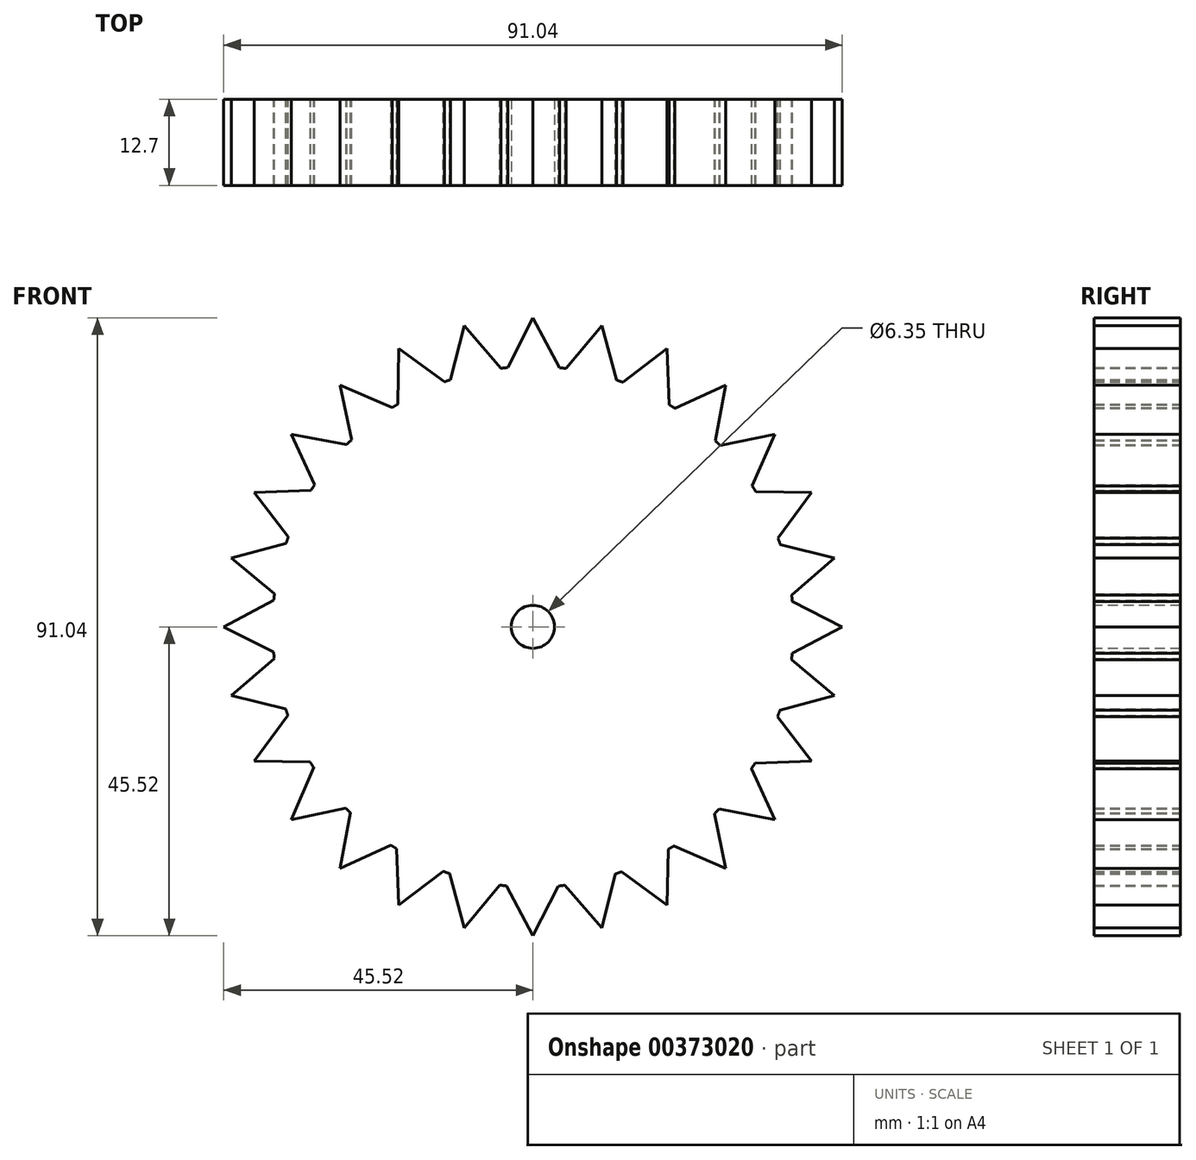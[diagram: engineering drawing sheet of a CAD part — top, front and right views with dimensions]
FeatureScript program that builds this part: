
annotation { "Feature Type Name" : "Feature", "Feature Type Description" : "" }
export const myFeature = defineFeature(function(context is Context, id is Id, definition is map)
    precondition{}
    {
        {
            var Q0;
            Q0=qCreatedBy(makeId("Front.planeOp"),FACE);
            var sketch = newSketch(context, id + "F0", { "sketchPlane" : qUnion([Q0])});
            skCircle(sketch, "E0", {"center": v(0, 0) * mm, "radius": 38.36 * mm});
            skLineSegment(sketch, "E1", {"start": v(-3.71, 38.18) * mm, "end": v(0, 45.52) * mm});
            skLineSegment(sketch, "E2", {"start": v(0, 45.52) * mm, "end": v(3.9, 38.16) * mm});
            skLineSegment(sketch, "E3.1.0", {"start": v(-10.13, 44.38) * mm, "end": v(-4.69, 38.08) * mm});
            skLineSegment(sketch, "E3.1.1", {"start": v(-12.12, 36.4) * mm, "end": v(-10.13, 44.38) * mm});
            skLineSegment(sketch, "E3.2.0", {"start": v(-19.75, 41.01) * mm, "end": v(-13.04, 36.08) * mm});
            skLineSegment(sketch, "E3.2.1", {"start": v(-19.91, 32.8) * mm, "end": v(-19.75, 41.01) * mm});
            skLineSegment(sketch, "E3.3.0", {"start": v(-28.38, 35.6) * mm, "end": v(-20.74, 32.27) * mm});
            skLineSegment(sketch, "E3.3.1", {"start": v(-26.7, 27.54) * mm, "end": v(-28.38, 35.6) * mm});
            skLineSegment(sketch, "E3.4.0", {"start": v(-35.6, 28.38) * mm, "end": v(-27.4, 26.85) * mm});
            skLineSegment(sketch, "E3.4.1", {"start": v(-32.17, 20.9) * mm, "end": v(-35.6, 28.38) * mm});
            skLineSegment(sketch, "E3.5.0", {"start": v(-41.01, 19.75) * mm, "end": v(-32.7, 20.07) * mm});
            skLineSegment(sketch, "E3.5.1", {"start": v(-36.01, 13.22) * mm, "end": v(-41.01, 19.75) * mm});
            skLineSegment(sketch, "E3.6.0", {"start": v(-44.38, 10.13) * mm, "end": v(-36.34, 12.3) * mm});
            skLineSegment(sketch, "E3.6.1", {"start": v(-38.05, 4.88) * mm, "end": v(-44.38, 10.13) * mm});
            skLineSegment(sketch, "E3.7.0", {"start": v(-45.52, 0) * mm, "end": v(-38.16, 3.9) * mm});
            skLineSegment(sketch, "E3.7.1", {"start": v(-38.18, -3.71) * mm, "end": v(-45.52, 0) * mm});
            skLineSegment(sketch, "E3.8.0", {"start": v(-44.38, -10.13) * mm, "end": v(-38.08, -4.69) * mm});
            skLineSegment(sketch, "E3.8.1", {"start": v(-36.4, -12.12) * mm, "end": v(-44.38, -10.13) * mm});
            skLineSegment(sketch, "E3.9.0", {"start": v(-41.01, -19.75) * mm, "end": v(-36.08, -13.04) * mm});
            skLineSegment(sketch, "E3.9.1", {"start": v(-32.8, -19.91) * mm, "end": v(-41.01, -19.75) * mm});
            skLineSegment(sketch, "E3.10.0", {"start": v(-35.6, -28.38) * mm, "end": v(-32.27, -20.74) * mm});
            skLineSegment(sketch, "E3.10.1", {"start": v(-27.54, -26.7) * mm, "end": v(-35.6, -28.38) * mm});
            skLineSegment(sketch, "E3.11.0", {"start": v(-28.38, -35.6) * mm, "end": v(-26.85, -27.4) * mm});
            skLineSegment(sketch, "E3.11.1", {"start": v(-20.9, -32.17) * mm, "end": v(-28.38, -35.6) * mm});
            skLineSegment(sketch, "E3.12.0", {"start": v(-19.75, -41.01) * mm, "end": v(-20.07, -32.7) * mm});
            skLineSegment(sketch, "E3.12.1", {"start": v(-13.22, -36.01) * mm, "end": v(-19.75, -41.01) * mm});
            skLineSegment(sketch, "E3.13.0", {"start": v(-10.13, -44.38) * mm, "end": v(-12.3, -36.34) * mm});
            skLineSegment(sketch, "E3.13.1", {"start": v(-4.88, -38.05) * mm, "end": v(-10.13, -44.38) * mm});
            skLineSegment(sketch, "E3.14.0", {"start": v(0, -45.52) * mm, "end": v(-3.9, -38.16) * mm});
            skLineSegment(sketch, "E3.14.1", {"start": v(3.71, -38.18) * mm, "end": v(0, -45.52) * mm});
            skLineSegment(sketch, "E3.15.0", {"start": v(10.13, -44.38) * mm, "end": v(4.69, -38.08) * mm});
            skLineSegment(sketch, "E3.15.1", {"start": v(12.12, -36.4) * mm, "end": v(10.13, -44.38) * mm});
            skLineSegment(sketch, "E3.16.0", {"start": v(19.75, -41.01) * mm, "end": v(13.04, -36.08) * mm});
            skLineSegment(sketch, "E3.16.1", {"start": v(19.91, -32.8) * mm, "end": v(19.75, -41.01) * mm});
            skLineSegment(sketch, "E3.17.0", {"start": v(28.38, -35.6) * mm, "end": v(20.74, -32.27) * mm});
            skLineSegment(sketch, "E3.17.1", {"start": v(26.7, -27.54) * mm, "end": v(28.38, -35.6) * mm});
            skLineSegment(sketch, "E3.18.0", {"start": v(35.6, -28.38) * mm, "end": v(27.4, -26.85) * mm});
            skLineSegment(sketch, "E3.18.1", {"start": v(32.17, -20.9) * mm, "end": v(35.6, -28.38) * mm});
            skLineSegment(sketch, "E3.19.0", {"start": v(41.01, -19.75) * mm, "end": v(32.7, -20.07) * mm});
            skLineSegment(sketch, "E3.19.1", {"start": v(36.01, -13.22) * mm, "end": v(41.01, -19.75) * mm});
            skLineSegment(sketch, "E3.20.0", {"start": v(44.38, -10.13) * mm, "end": v(36.34, -12.3) * mm});
            skLineSegment(sketch, "E3.20.1", {"start": v(38.05, -4.88) * mm, "end": v(44.38, -10.13) * mm});
            skLineSegment(sketch, "E3.21.0", {"start": v(45.52, 0) * mm, "end": v(38.16, -3.9) * mm});
            skLineSegment(sketch, "E3.21.1", {"start": v(38.18, 3.71) * mm, "end": v(45.52, 0) * mm});
            skLineSegment(sketch, "E3.22.0", {"start": v(44.38, 10.13) * mm, "end": v(38.08, 4.69) * mm});
            skLineSegment(sketch, "E3.22.1", {"start": v(36.4, 12.12) * mm, "end": v(44.38, 10.13) * mm});
            skLineSegment(sketch, "E3.23.0", {"start": v(41.01, 19.75) * mm, "end": v(36.08, 13.04) * mm});
            skLineSegment(sketch, "E3.23.1", {"start": v(32.8, 19.91) * mm, "end": v(41.01, 19.75) * mm});
            skLineSegment(sketch, "E3.24.0", {"start": v(35.6, 28.38) * mm, "end": v(32.27, 20.74) * mm});
            skLineSegment(sketch, "E3.24.1", {"start": v(27.54, 26.7) * mm, "end": v(35.6, 28.38) * mm});
            skLineSegment(sketch, "E3.25.0", {"start": v(28.38, 35.6) * mm, "end": v(26.85, 27.4) * mm});
            skLineSegment(sketch, "E3.25.1", {"start": v(20.9, 32.17) * mm, "end": v(28.38, 35.6) * mm});
            skLineSegment(sketch, "E3.26.0", {"start": v(19.75, 41.01) * mm, "end": v(20.07, 32.7) * mm});
            skLineSegment(sketch, "E3.26.1", {"start": v(13.22, 36.01) * mm, "end": v(19.75, 41.01) * mm});
            skLineSegment(sketch, "E3.27.0", {"start": v(10.13, 44.38) * mm, "end": v(12.3, 36.34) * mm});
            skLineSegment(sketch, "E3.27.1", {"start": v(4.88, 38.05) * mm, "end": v(10.13, 44.38) * mm});
            skSolve(sketch);
        }
        {
            var Q0;
            Q0 = qSketchRegion(id + "F0", true);
            extrude(context, id + "F1", {"entities" : qUnion([Q0]), "depth" : 12.7 * mm});
        }
        {
            var Q0;
            Q0=makeQuery(id+"F1.opExtrude","CAP_FACE",FACE,{"disambiguationData":[OSD([sQuery(id+"F0.wireOp",EDGE,"E0"),sQuery(id+"F0.wireOp",EDGE,"E1"),sQuery(id+"F0.wireOp",EDGE,"E2"),sQuery(id+"F0.wireOp",EDGE,"E3.1.0"),sQuery(id+"F0.wireOp",EDGE,"E3.1.1"),sQuery(id+"F0.wireOp",EDGE,"E3.2.0"),sQuery(id+"F0.wireOp",EDGE,"E3.2.1"),sQuery(id+"F0.wireOp",EDGE,"E3.3.0"),sQuery(id+"F0.wireOp",EDGE,"E3.3.1"),sQuery(id+"F0.wireOp",EDGE,"E3.4.0"),sQuery(id+"F0.wireOp",EDGE,"E3.4.1"),sQuery(id+"F0.wireOp",EDGE,"E3.5.0"),sQuery(id+"F0.wireOp",EDGE,"E3.5.1"),sQuery(id+"F0.wireOp",EDGE,"E3.6.0"),sQuery(id+"F0.wireOp",EDGE,"E3.6.1"),sQuery(id+"F0.wireOp",EDGE,"E3.7.0"),sQuery(id+"F0.wireOp",EDGE,"E3.7.1"),sQuery(id+"F0.wireOp",EDGE,"E3.8.0"),sQuery(id+"F0.wireOp",EDGE,"E3.8.1"),sQuery(id+"F0.wireOp",EDGE,"E3.9.0"),sQuery(id+"F0.wireOp",EDGE,"E3.9.1"),sQuery(id+"F0.wireOp",EDGE,"E3.10.0"),sQuery(id+"F0.wireOp",EDGE,"E3.10.1"),sQuery(id+"F0.wireOp",EDGE,"E3.11.0"),sQuery(id+"F0.wireOp",EDGE,"E3.11.1"),sQuery(id+"F0.wireOp",EDGE,"E3.12.0"),sQuery(id+"F0.wireOp",EDGE,"E3.12.1"),sQuery(id+"F0.wireOp",EDGE,"E3.13.0"),sQuery(id+"F0.wireOp",EDGE,"E3.13.1"),sQuery(id+"F0.wireOp",EDGE,"E3.14.0"),sQuery(id+"F0.wireOp",EDGE,"E3.14.1"),sQuery(id+"F0.wireOp",EDGE,"E3.15.0"),sQuery(id+"F0.wireOp",EDGE,"E3.15.1"),sQuery(id+"F0.wireOp",EDGE,"E3.16.0"),sQuery(id+"F0.wireOp",EDGE,"E3.16.1"),sQuery(id+"F0.wireOp",EDGE,"E3.17.0"),sQuery(id+"F0.wireOp",EDGE,"E3.17.1"),sQuery(id+"F0.wireOp",EDGE,"E3.18.0"),sQuery(id+"F0.wireOp",EDGE,"E3.18.1"),sQuery(id+"F0.wireOp",EDGE,"E3.19.0"),sQuery(id+"F0.wireOp",EDGE,"E3.19.1"),sQuery(id+"F0.wireOp",EDGE,"E3.20.0"),sQuery(id+"F0.wireOp",EDGE,"E3.20.1"),sQuery(id+"F0.wireOp",EDGE,"E3.21.0"),sQuery(id+"F0.wireOp",EDGE,"E3.21.1"),sQuery(id+"F0.wireOp",EDGE,"E3.22.0"),sQuery(id+"F0.wireOp",EDGE,"E3.22.1"),sQuery(id+"F0.wireOp",EDGE,"E3.23.0"),sQuery(id+"F0.wireOp",EDGE,"E3.23.1"),sQuery(id+"F0.wireOp",EDGE,"E3.24.0"),sQuery(id+"F0.wireOp",EDGE,"E3.24.1"),sQuery(id+"F0.wireOp",EDGE,"E3.25.0"),sQuery(id+"F0.wireOp",EDGE,"E3.25.1"),sQuery(id+"F0.wireOp",EDGE,"E3.26.0"),sQuery(id+"F0.wireOp",EDGE,"E3.26.1"),sQuery(id+"F0.wireOp",EDGE,"E3.27.0"),sQuery(id+"F0.wireOp",EDGE,"E3.27.1")])],"isStart":false});
            var sketch = newSketch(context, id + "F2", { "sketchPlane" : qUnion([Q0])});
            skCircle(sketch, "E4", {"center": v(0, 0) * mm, "radius": 3.18 * mm});
            skSolve(sketch);
        }
        {
            var Q0;
            Q0 = qSketchRegion(id + "F2", true);
            extrude(context, id + "F3", {"entities" : qUnion([Q0]), "operationType" : NewBodyOperationType.REMOVE, "oppositeDirection" : true, "depth" : 25.4 * mm});
        }
    });
